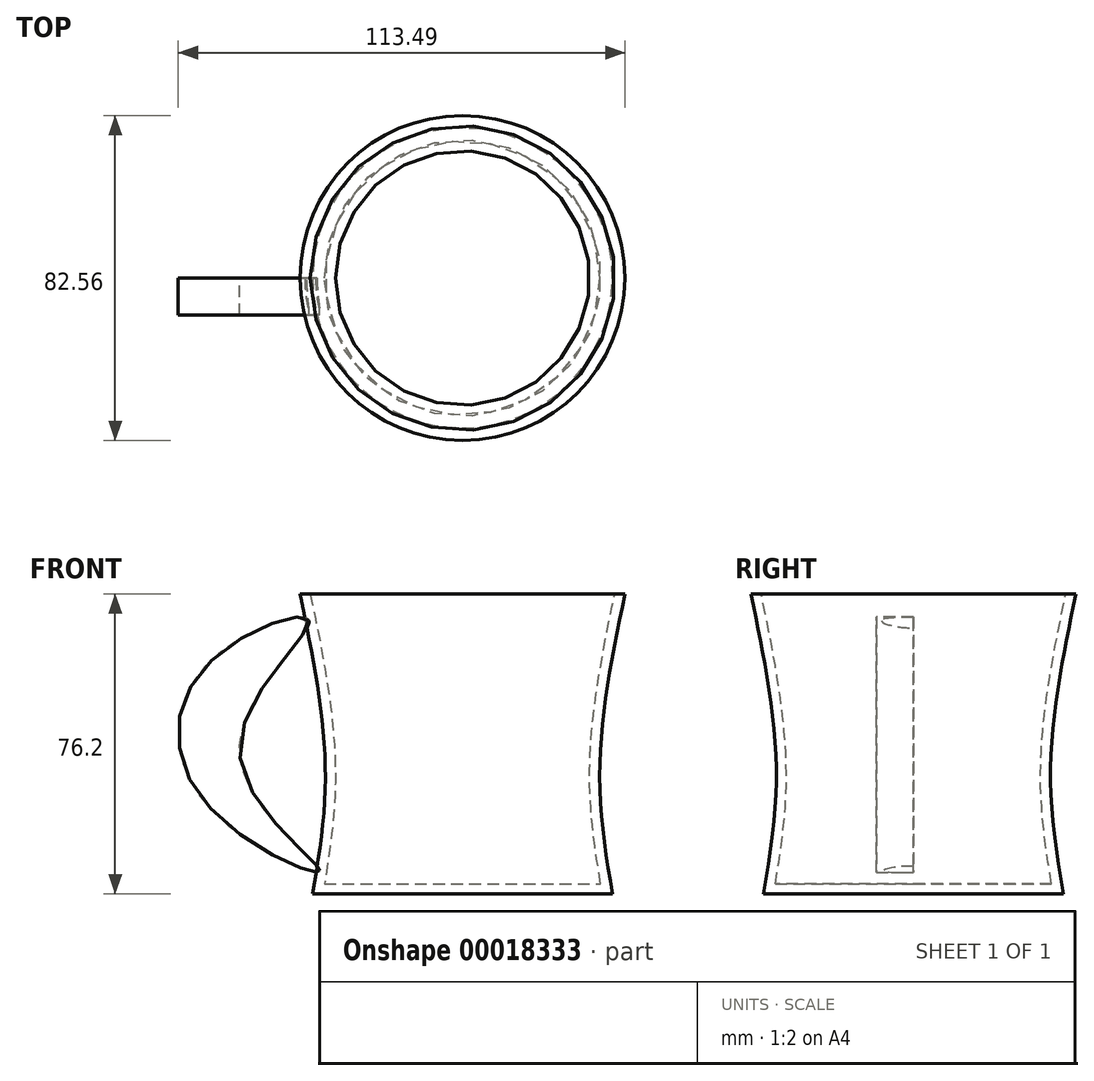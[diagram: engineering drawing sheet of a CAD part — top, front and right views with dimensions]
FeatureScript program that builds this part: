
annotation { "Feature Type Name" : "Feature", "Feature Type Description" : "" }
export const myFeature = defineFeature(function(context is Context, id is Id, definition is map)
    precondition{}
    {
        {
            var Q0;
            Q0=qCreatedBy(makeId("Top.planeOp"),FACE);
            var sketch = newSketch(context, id + "F0", { "sketchPlane" : qUnion([Q0])});
            skCircle(sketch, "E0", {"center": v(0, 0) * mm, "radius": 38.1 * mm});
            skSolve(sketch);
        }
        {
            var Q0;
            Q0=qCreatedBy(makeId("Top.planeOp"),FACE);
            cPlane(context, id + "F1", {"entities" : qUnion([Q0]), "cplaneType" : CPlaneType.OFFSET, "offset" : 25.4 * mm, "width" : 152.4 * mm, "height" : 152.4 * mm});
        }
        {
            var Q0;
            Q0=qCreatedBy(id+"F1.planeOp",FACE);
            var sketch = newSketch(context, id + "F2", { "sketchPlane" : qUnion([Q0])});
            skPoint(sketch, "E1.0", {"position": v(0, 0) * mm});
            skCircle(sketch, "E2", {"center": v(0, 0) * mm, "radius": 34.93 * mm});
            skSolve(sketch);
        }
        {
            var Q0;
            Q0=qCreatedBy(makeId("Top.planeOp"),FACE);
            cPlane(context, id + "F3", {"entities" : qUnion([Q0]), "cplaneType" : CPlaneType.OFFSET, "offset" : 76.2 * mm, "width" : 152.4 * mm, "height" : 152.4 * mm});
        }
        {
            var Q0;
            Q0=qCreatedBy(id+"F3.planeOp",FACE);
            var sketch = newSketch(context, id + "F4", { "sketchPlane" : qUnion([Q0])});
            skPoint(sketch, "E3.0", {"position": v(0, 0) * mm});
            skCircle(sketch, "E4", {"center": v(0, 0) * mm, "radius": 41.28 * mm});
            skSolve(sketch);
        }
        {
            var Q0;
            Q0=makeQuery(id+"F4.imprint","IMPRINT",FACE,{"disambiguationData":[TD([[makeQuery(id+"F4.imprint","IMPRINT",EDGE,{"derivedFrom":sQuery(id+"F4.wireOp",EDGE,"E4")}),1.0]])]});
            var Q1;
            Q1=makeQuery(id+"F2.imprint","IMPRINT",FACE,{"disambiguationData":[TD([[makeQuery(id+"F2.imprint","IMPRINT",EDGE,{"derivedFrom":sQuery(id+"F2.wireOp",EDGE,"E2")}),1.0]])]});
            var Q2;
            Q2=makeQuery(id+"F0.imprint","IMPRINT",FACE,{"disambiguationData":[TD([[makeQuery(id+"F0.imprint","IMPRINT",EDGE,{"derivedFrom":sQuery(id+"F0.wireOp",EDGE,"E0")}),1.0]])]});
            loft(context, id + "F5", {"sheetProfilesArray" : [{ "sheetProfileEntities" : qUnion([Q0]) }, { "sheetProfileEntities" : qUnion([Q1]) }, { "sheetProfileEntities" : qUnion([Q2]) }]});
        }
        {
            var Q0;
            Q0=makeQuery(id+"F5.opLoft","CAP_FACE",FACE,{"disambiguationData":[OSD([makeQuery(id+"F4.imprint","IMPRINT",FACE,{"disambiguationData":[TD([[makeQuery(id+"F4.imprint","IMPRINT",EDGE,{"derivedFrom":sQuery(id+"F4.wireOp",EDGE,"E4")}),1.0]])]})])],"isStart":true});
            shell(context, id + "F6", {"entities" : qUnion([Q0]), "thickness" : 2.54 * mm});
        }
        {
            var Q0;
            Q0=qCreatedBy(makeId("Front.planeOp"),FACE);
            var sketch = newSketch(context, id + "F7", { "sketchPlane" : qUnion([Q0])});
            skFitSpline(sketch, "E5", {"points": [v(-39.05, 69.5) * mm, v(-65, 58.16) * mm, v(-64.7, 22.4) * mm, v(-36.33, 5.87) * mm, v(-56.62, 35.89) * mm, v(-39.05, 69.5) * mm]});
            skSolve(sketch);
        }
        {
            var Q0;
            Q0=makeQuery(id+"F7.imprint","IMPRINT",FACE,{"disambiguationData":[TD([[makeQuery(id+"F7.imprint","IMPRINT",EDGE,{"derivedFrom":sQuery(id+"F7.wireOp",EDGE,"E5")}),1.0]])]});
            extrude(context, id + "F8", {"entities" : qUnion([Q0]), "operationType" : NewBodyOperationType.ADD, "depth" : 9.45 * mm});
        }
    });
